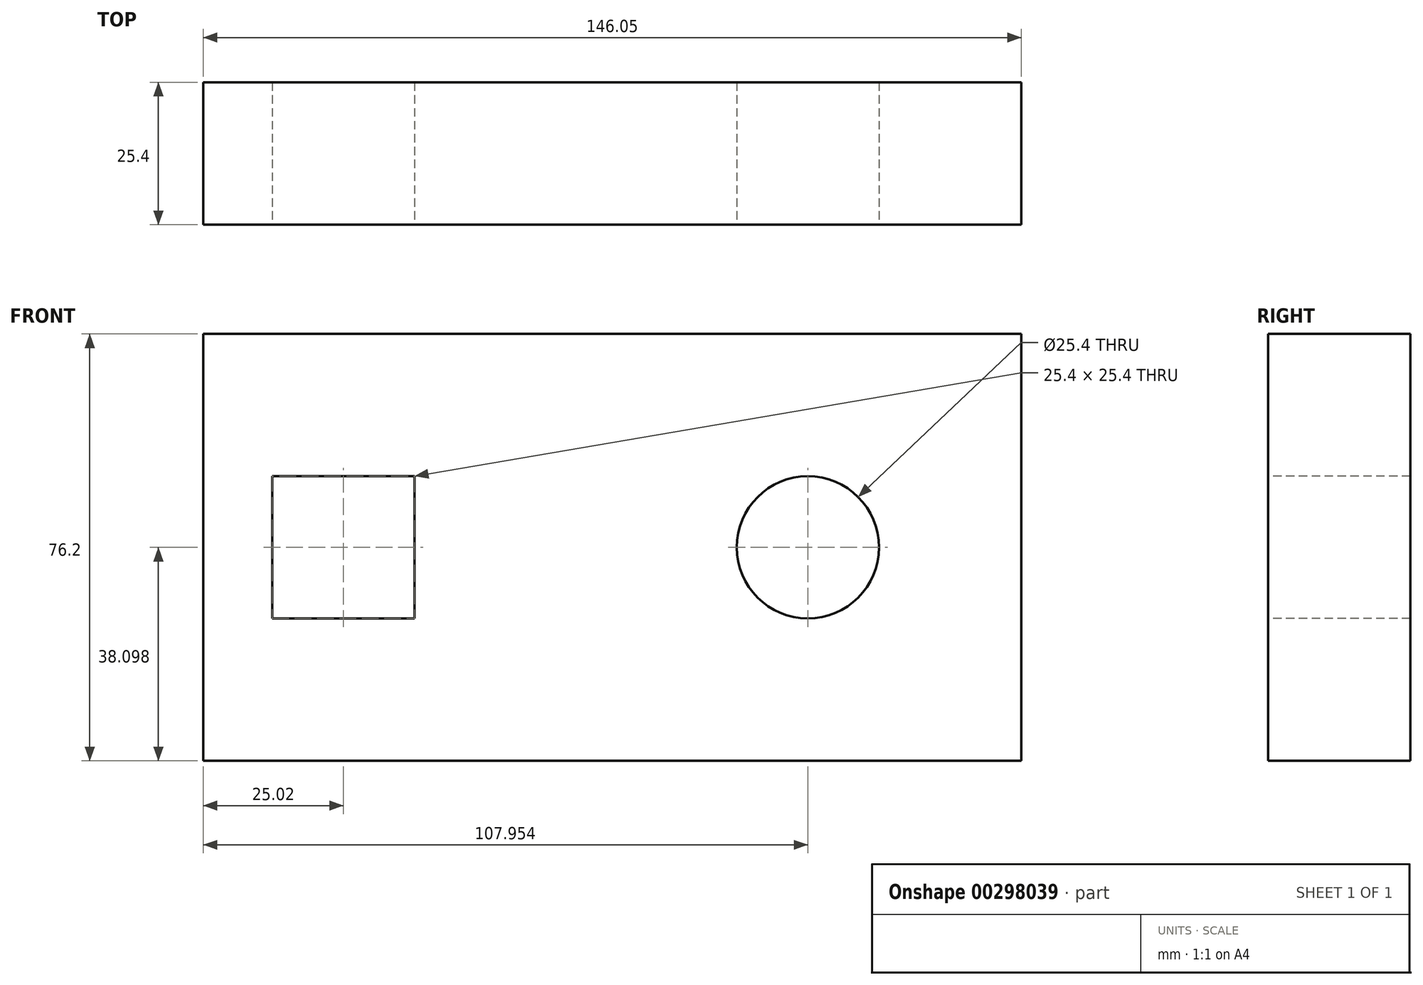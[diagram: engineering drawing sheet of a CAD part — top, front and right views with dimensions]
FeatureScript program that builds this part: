
annotation { "Feature Type Name" : "Feature", "Feature Type Description" : "" }
export const myFeature = defineFeature(function(context is Context, id is Id, definition is map)
    precondition{}
    {
        {
            var Q0;
            Q0=qCreatedBy(makeId("Front.planeOp"),FACE);
            var sketch = newSketch(context, id + "F0", { "sketchPlane" : qUnion([Q0])});
            skLineSegment(sketch, "E0.bottom", {"start": v(-159.23, 103.89) * mm, "end": v(-13.18, 103.89) * mm});
            skLineSegment(sketch, "E0.top", {"start": v(-159.23, 27.69) * mm, "end": v(-13.18, 27.69) * mm});
            skLineSegment(sketch, "E0.left", {"start": v(-159.23, 103.89) * mm, "end": v(-159.23, 27.69) * mm});
            skLineSegment(sketch, "E0.right", {"start": v(-13.18, 103.89) * mm, "end": v(-13.18, 27.69) * mm});
            skSolve(sketch);
        }
        {
            var Q0;
            Q0 = qSketchRegion(id + "F0", true);
            extrude(context, id + "F1", {"entities" : qUnion([Q0]), "depth" : 25.4 * mm});
        }
        {
            var Q0;
            Q0=makeQuery(id+"F1.opExtrude","CAP_FACE",FACE,{"disambiguationData":[OSD([sQuery(id+"F0.wireOp",EDGE,"E0.bottom"),sQuery(id+"F0.wireOp",EDGE,"E0.top"),sQuery(id+"F0.wireOp",EDGE,"E0.left"),sQuery(id+"F0.wireOp",EDGE,"E0.right")])],"isStart":false});
            var sketch = newSketch(context, id + "F2", { "sketchPlane" : qUnion([Q0])});
            skLineSegment(sketch, "E1.bottom", {"start": v(-146.9, 78.49) * mm, "end": v(-121.5, 78.49) * mm});
            skLineSegment(sketch, "E1.top", {"start": v(-146.9, 53.09) * mm, "end": v(-121.5, 53.09) * mm});
            skLineSegment(sketch, "E1.left", {"start": v(-146.9, 78.49) * mm, "end": v(-146.9, 53.09) * mm});
            skLineSegment(sketch, "E1.right", {"start": v(-121.5, 78.49) * mm, "end": v(-121.5, 53.09) * mm});
            skArc(sketch, "E2", {"start": v(-38.59, 65.25) * mm, "mid": v(-63.96, 66.47) * mm, "end": v(-38.6, 64.96) * mm});
            skArc(sketch, "E3", {"start": v(-38.6, 64.96) * mm, "mid": v(-38.6, 65.1) * mm, "end": v(-38.59, 65.25) * mm});
            skSolve(sketch);
        }
        {
            var Q0;
            Q0=makeQuery(id+"F2.imprint","IMPRINT",FACE,{"disambiguationData":[TD([[makeQuery(id+"F2.imprint","IMPRINT",EDGE,{"derivedFrom":sQuery(id+"F2.wireOp",EDGE,"E1.bottom")}),-1.0]])]});
            var Q1;
            Q1=makeQuery(id+"F2.imprint","IMPRINT",FACE,{"disambiguationData":[TD([[makeQuery(id+"F2.imprint","IMPRINT",EDGE,{"derivedFrom":sQuery(id+"F2.wireOp",EDGE,"E2")}),1.0]])]});
            extrude(context, id + "F3", {"entities" : qUnion([Q0, Q1]), "operationType" : NewBodyOperationType.REMOVE, "oppositeDirection" : true, "depth" : 25.4 * mm});
        }
    });
